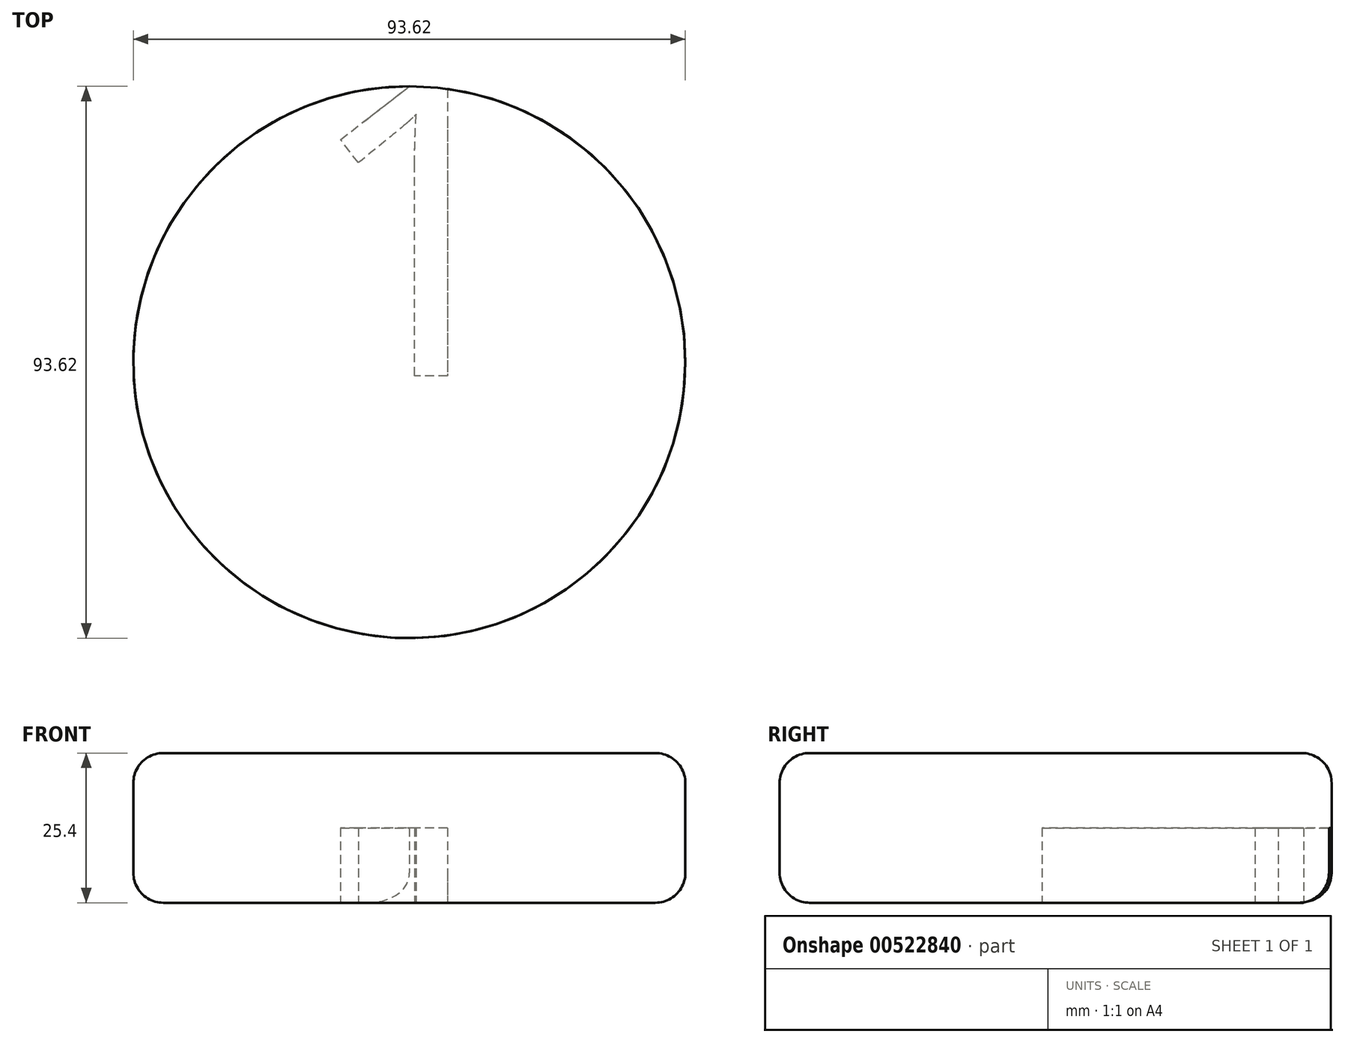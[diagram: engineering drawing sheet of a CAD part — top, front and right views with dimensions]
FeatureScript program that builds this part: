
annotation { "Feature Type Name" : "Feature", "Feature Type Description" : "" }
export const myFeature = defineFeature(function(context is Context, id is Id, definition is map)
    precondition{}
    {
        {
            var Q0;
            Q0=qCreatedBy(makeId("Top.planeOp"),FACE);
            var sketch = newSketch(context, id + "F0", { "sketchPlane" : qUnion([Q0])});
            skCircle(sketch, "E0", {"center": v(0, 0) * mm, "radius": 46.81 * mm});
            skSolve(sketch);
        }
        {
            var Q0;
            Q0 = qSketchRegion(id + "F0", true);
            extrude(context, id + "F1", {"entities" : qUnion([Q0]), "depth" : 25.4 * mm, "offsetDistance" : 25.4 * mm});
        }
        {
            var Q0;
            Q0=makeQuery(id+"F1.opExtrude","CAP_EDGE",EDGE,{"disambiguationData":[OSD([sQuery(id+"F0.wireOp",EDGE,"E0")])],"isStart":true});
            var Q1;
            Q1=makeQuery(id+"F1.opExtrude","CAP_EDGE",EDGE,{"disambiguationData":[OSD([sQuery(id+"F0.wireOp",EDGE,"E0")])],"isStart":false});
            fillet(context, id + "F2", {"entities" : qUnion([Q0, Q1]), "radius" : 5.08 * mm, "tangentPropagation" : true, "allowEdgeOverflow" : false});
        }
        {
            var Q0;
            Q0=qCreatedBy(makeId("Top.planeOp"),FACE);
            var sketch = newSketch(context, id + "F3", { "sketchPlane" : qUnion([Q0])});
            skText(sketch, "E1", { "text": "1", "fontName": "OpenSans-Regular.ttf"});
            const initialGuessF3  = {"E1": [-0.01816, -0.0023, 1, 0, 0.0508]};
            skSetInitialGuess(sketch, initialGuessF3);
            skSolve(sketch);
        }
        {
            var Q0;
            Q0 = qSketchRegion(id + "F3", true);
            extrude(context, id + "F4", {"entities" : qUnion([Q0]), "operationType" : NewBodyOperationType.REMOVE, "depth" : 12.7 * mm, "offsetDistance" : 25.4 * mm});
        }
    });
